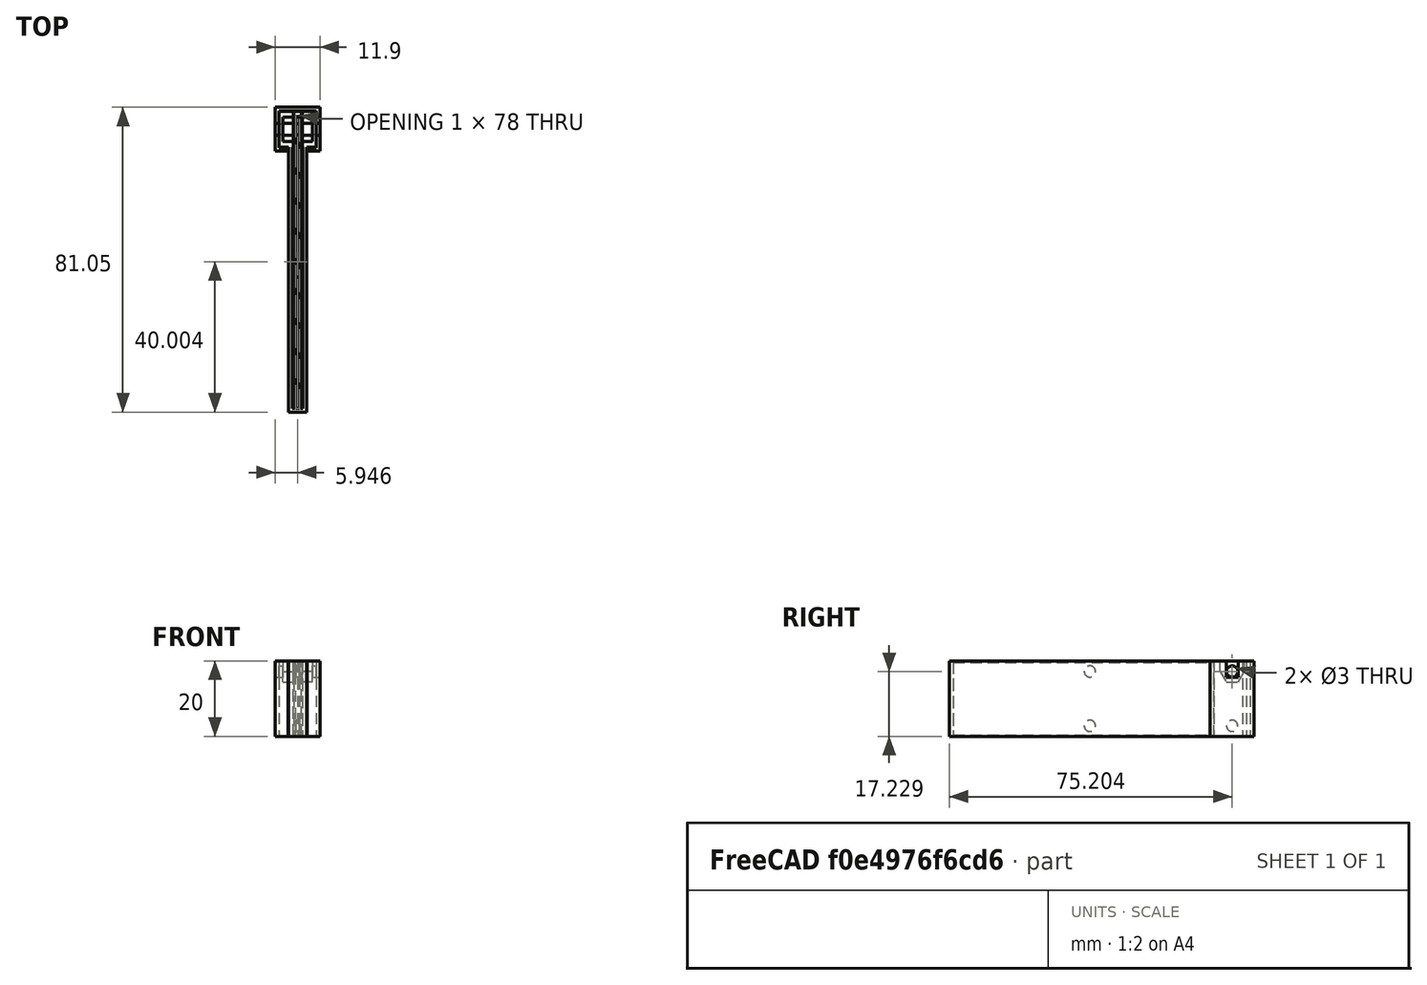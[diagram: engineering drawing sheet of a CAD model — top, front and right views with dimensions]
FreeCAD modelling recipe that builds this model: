
FCSTD DOCUMENT  (FreeCAD 0.20R29177 +233 (Git))
Label: capacitor
License: All rights reserved
LicenseURL: http://en.wikipedia.org/wiki/All_rights_reserved
objects: Part::Part2DObjectPython×31, Part::Extrusion×30, Part::Cut×20, Part::MultiFuse×7, Part::Refine×2, Part::Feature×2, Part::FeaturePython×1
note: 93 computed .brp shape members not serialized (recipe doc carries the construction recipe); baked Part::Feature solids carry a one-line shape summary decoded from their .brp

FEATURE [Part::Part2DObjectPython] Rectangle  # Draft 2D object (typed FeaturePython)
  Area = 1600
  ChamferSize = 0
  Columns = 1
  FilletRadius = 0
  Height = 80
  Length = 20
  MakeFace = true
  Placement = pos=(-3.02724,-4.37282,1) rot=(0,0,1;0rad)
  Rows = 1
FEATURE [Part::Part2DObjectPython] Rectangle001  # Draft 2D object (typed FeaturePython)
  Area = 1804
  ChamferSize = 0
  Columns = 1
  FilletRadius = 0
  Height = 82
  Length = 22
  MakeFace = true
  Placement = pos=(-4.02724,-5.37282,0) rot=(0,0,1;0rad)
  Rows = 1
FEATURE [Part::Part2DObjectPython] Rectangle002  # Draft 2D object (typed FeaturePython)
  Area = 400
  ChamferSize = 0
  Columns = 1
  FilletRadius = 0
  Height = 20
  Length = 20
  MakeFace = true
  Placement = pos=(46.4257,-3.50556,0.5) rot=(0,0,1;0rad)
  Rows = 1
FEATURE [Part::Extrusion] Extrusion002
  Base = -> Rectangle002
  Dir = (0,0,-80)
  DirMode = 0
  FaceMakerClass = Part::FaceMakerBullseye
  LengthFwd = 0
  LengthRev = 0
  Solid = true
  Symmetric = false
FEATURE [Part::Part2DObjectPython] Rectangle004  # Draft 2D object (typed FeaturePython)
  Area = 6
  ChamferSize = 0
  Columns = 1
  FilletRadius = 0
  Height = 30
  Length = 0.2
  MakeFace = true
  Placement = pos=(51.3257,-13.5056,0.5) rot=(0,0,1;0rad)
  Rows = 1
FEATURE [Part::Part2DObjectPython] Clone2D  label="Rectangle004 (2D)"  # Draft 2D object (typed FeaturePython)
  Fuse = false
  Objects = -> [Rectangle004]
  Placement = pos=(53.5257,-13.5056,0.5) rot=(0,0,1;0rad)
  Scale = (1,1,1)
FEATURE [Part::Extrusion] Extrusion003
  Base = -> Rectangle004
  Dir = (0,0,-79)
  DirMode = 0
  FaceMakerClass = Part::FaceMakerBullseye
  LengthFwd = 0
  LengthRev = 0
  Solid = true
  Symmetric = false
FEATURE [Part::Extrusion] Extrusion004
  Base = -> Clone2D
  Dir = (0,0,-79)
  DirMode = 0
  FaceMakerClass = Part::FaceMakerBullseye
  LengthFwd = 0
  LengthRev = 0
  Solid = true
  Symmetric = false
FEATURE [Part::Cut] Cut001
  Base = -> Extrusion002
  Tool = -> Extrusion004
FEATURE [Part::Cut] Cut002
  Base = -> Cut001
  Tool = -> Extrusion003
FEATURE [Part::Part2DObjectPython] Rectangle005  # Draft 2D object (typed FeaturePython)
  Area = 200.96
  ChamferSize = 0
  Columns = 1
  FilletRadius = 0
  Height = 200.96
  Length = 1
  MakeFace = true
  Placement = pos=(53.0257,101.974,0.5) rot=(0,0,1;3.14159rad)
  Rows = 1
FEATURE [Part::Extrusion] Extrusion005
  Base = -> Rectangle005
  Dir = (0,0,-79)
  DirMode = 0
  FaceMakerClass = Part::FaceMakerBullseye
  LengthFwd = 0
  LengthRev = 0
  Solid = true
  Symmetric = false
FEATURE [Part::Cut] Cut003
  Base = -> Cut002
  Tool = -> Extrusion005
FEATURE [Part::Part2DObjectPython] Rectangle006  # Draft 2D object (typed FeaturePython)
  Area = 20
  ChamferSize = 0
  Columns = 1
  FilletRadius = 0
  Height = 1
  Length = 20
  MakeFace = true
  Placement = pos=(53.0257,-3.50556,0.5) rot=(0,0,1;1.5708rad)
  Rows = 1
FEATURE [Part::Part2DObjectPython] Rectangle007  # Draft 2D object (typed FeaturePython)
  Area = 2
  ChamferSize = 0
  Columns = 1
  FilletRadius = 0
  Height = 2
  Length = 1
  MakeFace = true
  Placement = pos=(52.0257,-3.50556,-1.5) rot=(1,0,0;1.5708rad)
  Rows = 1
FEATURE [Part::Part2DObjectPython] Wire  # Draft 2D object (typed FeaturePython)
  Area = 0.5
  ChamferSize = 0
  Closed = true
  End = (53.0257,-3.50556,-1.5)
  FilletRadius = 0
  Length = 3.23607
  MakeFace = true
  Placement = pos=(52.0257,-3.50556,-1.5) rot=(1,0,0;1.5708rad)
  Points = (3) [(0,0,0),(0.5,1,0),(1,0,0)]
  Start = (52.0257,-3.50556,-1.5)
  Subdivisions = 0
FEATURE [Part::Extrusion] Extrusion006
  Base = -> Wire
  Dir = (-4e-16,55.9863,-1.24e-14)
  DirMode = 0
  FaceMakerClass = Part::FaceMakerBullseye
  LengthFwd = 0
  LengthRev = 0
  Solid = true
  Symmetric = false
FEATURE [Part::Extrusion] Extrusion007
  Base = -> Rectangle006
  Dir = (0,0,-2)
  DirMode = 0
  FaceMakerClass = Part::FaceMakerBullseye
  LengthFwd = 0
  LengthRev = 0
  Solid = true
  Symmetric = false
FEATURE [Part::Cut] Cut004
  Base = -> Extrusion007
  Tool = -> Extrusion006
FEATURE [Part::MultiFuse] Fusion
  Shapes = -> [Cut004,Cut003]
FEATURE [Part::Part2DObjectPython] Rectangle008  # Draft 2D object (typed FeaturePython)
  Area = 156
  ChamferSize = 0
  Columns = 1
  FilletRadius = 0
  Height = 20
  Length = 7.8
  MakeFace = true
  Placement = pos=(66.4257,16.4944,0.5) rot=(0,0,1;3.14159rad)
  Rows = 1
FEATURE [Part::Extrusion] Extrusion008
  Base = -> Rectangle008
  Dir = (0,0,-104.818)
  DirMode = 0
  FaceMakerClass = Part::FaceMakerBullseye
  LengthFwd = 0
  LengthRev = 0
  Solid = true
  Symmetric = false
FEATURE [Part::Cut] Cut005
  Base = -> Fusion
  Placement = pos=(0,95.9944,-63.0056) rot=(1,0,0;4.71239rad)
  Tool = -> Extrusion008
FEATURE [Part::Part2DObjectPython] Rectangle009  # Draft 2D object (typed FeaturePython)
  Area = 1550.5
  ChamferSize = 0
  Columns = 1
  FilletRadius = 0
  Height = 103.264
  Length = 15.0148
  MakeFace = true
  Placement = pos=(33.8608,-6.76991,-59.5) rot=(0,0,1;0rad)
  Rows = 1
FEATURE [Part::Part2DObjectPython] Rectangle010  # Draft 2D object (typed FeaturePython)
  Area = 974.157
  ChamferSize = 0
  Columns = 1
  FilletRadius = 0
  Height = 103.122
  Length = 9.44666
  MakeFace = true
  Placement = pos=(56.1757,-6.62743,-59.5) rot=(0,0,1;0rad)
  Rows = 1
FEATURE [Part::Extrusion] Extrusion009
  Base = -> Rectangle009
  Dir = (-3.6e-15,-1.79e-14,-80.6023)
  DirMode = 0
  FaceMakerClass = Part::FaceMakerBullseye
  LengthFwd = 0
  LengthRev = 0
  Solid = true
  Symmetric = false
FEATURE [Part::Extrusion] Extrusion010
  Base = -> Rectangle010
  Dir = (-3.6e-15,-1.79e-14,-80.6023)
  DirMode = 0
  FaceMakerClass = Part::FaceMakerBullseye
  LengthFwd = 0
  LengthRev = 0
  Solid = true
  Symmetric = false
FEATURE [Part::Cut] Cut006
  Base = -> Cut005
  Tool = -> Extrusion009
FEATURE [Part::Cut] Cut007
  Base = -> Cut006
  Tool = -> Extrusion010
FEATURE [Part::Part2DObjectPython] Polygon  # Draft 2D object (typed FeaturePython)
  Area = 26.6043
  ChamferSize = 0
  DrawMode = 0
  FacesNumber = 6
  FilletRadius = 0
  MakeFace = true
  Placement = pos=(48.6257,91.6944,-62.2713) rot=(0.57735,0.57735,0.57735;2.0944rad)
  Radius = 3.2
FEATURE [Part::Part2DObjectPython] Clone2D001  label="Polygon (2D)"  # Draft 2D object (typed FeaturePython)
  Fuse = false
  Objects = -> [Polygon]
  Placement = pos=(56.4257,91.6944,-62.2713) rot=(0.57735,0.57735,0.57735;2.0944rad)
  Scale = (1,1,1)
FEATURE [Part::Part2DObjectPython] Rectangle011  # Draft 2D object (typed FeaturePython)
  Area = 192
  ChamferSize = 0
  Columns = 1
  FilletRadius = 0
  Height = 20
  Length = 9.6
  MakeFace = true
  Placement = pos=(56.1757,86.8944,-79.5) rot=(0.57735,0.57735,0.57735;2.0944rad)
  Rows = 1
FEATURE [Part::Part2DObjectPython] Clone2D002  label="Rectangle011 (2D)"  # Draft 2D object (typed FeaturePython)
  Fuse = false
  Objects = -> [Rectangle011]
  Placement = pos=(48.8757,86.8944,-79.5) rot=(0.57735,0.57735,0.57735;2.0944rad)
  Scale = (1,1,1)
FEATURE [Part::Extrusion] Extrusion011
  Base = -> Rectangle011
  Dir = (0.25,1e-16,0)
  DirMode = 0
  FaceMakerClass = Part::FaceMakerBullseye
  LengthFwd = 0
  LengthRev = 0
  Solid = true
  Symmetric = false
FEATURE [Part::MultiFuse] Fusion001
  Shapes = -> [Cut007,Extrusion011]
FEATURE [Part::Extrusion] Extrusion012
  Base = -> Clone2D002
  Dir = (-0.25,-1e-16,0)
  DirMode = 0
  FaceMakerClass = Part::FaceMakerBullseye
  LengthFwd = 0
  LengthRev = 0
  Solid = true
  Symmetric = false
FEATURE [Part::MultiFuse] Fusion002
  Shapes = -> [Extrusion012,Fusion001]
FEATURE [Part::Extrusion] Extrusion013
  Base = -> Clone2D001
  Dir = (-2.7,0,-6e-16)
  DirMode = 0
  FaceMakerClass = Part::FaceMakerBullseye
  LengthFwd = 0
  LengthRev = 0
  Solid = true
  Symmetric = false
FEATURE [Part::Cut] Cut008
  Base = -> Fusion002
  Tool = -> Extrusion013
FEATURE [Part::Extrusion] Extrusion014
  Base = -> Polygon
  Dir = (2.7,0,6e-16)
  DirMode = 0
  FaceMakerClass = Part::FaceMakerBullseye
  LengthFwd = 0
  LengthRev = 0
  Solid = true
  Symmetric = false
FEATURE [Part::Cut] Cut009
  Base = -> Cut008
  Tool = -> Extrusion014
FEATURE [Part::Part2DObjectPython] Rectangle012  # Draft 2D object (typed FeaturePython)
  Area = 17.7362
  ChamferSize = 0
  Columns = 1
  FilletRadius = 0
  Height = 2.77128
  Length = 6.4
  MakeFace = true
  Placement = pos=(48.6257,94.8944,-62.2713) rot=(0.57735,-0.57735,-0.57735;2.0944rad)
  Rows = 1
FEATURE [Part::Extrusion] Extrusion015
  Base = -> Rectangle012
  Dir = (2.7,0,0)
  DirMode = 0
  FaceMakerClass = Part::FaceMakerBullseye
  LengthFwd = 0
  LengthRev = 0
  Solid = true
  Symmetric = false
FEATURE [Part::Cut] Cut010
  Base = -> Cut009
  Tool = -> Extrusion015
FEATURE [Part::Part2DObjectPython] Rectangle013  # Draft 2D object (typed FeaturePython)
  Area = 17.7362
  ChamferSize = 0
  Columns = 1
  FilletRadius = 0
  Height = 2.77128
  Length = 6.4
  MakeFace = true
  Placement = pos=(56.4257,88.4944,-62.2713) rot=(0.57735,0.57735,0.57735;2.0944rad)
  Rows = 1
FEATURE [Part::Extrusion] Extrusion016
  Base = -> Rectangle013
  Dir = (-2.7,0,0)
  DirMode = 0
  FaceMakerClass = Part::FaceMakerBullseye
  LengthFwd = 0
  LengthRev = 0
  Solid = true
  Symmetric = false
FEATURE [Part::Cut] Cut011
  Base = -> Cut010
  Tool = -> Extrusion016
FEATURE [Part::Part2DObjectPython] Rectangle014  # Draft 2D object (typed FeaturePython)
  Area = 192
  ChamferSize = 0
  Columns = 1
  FilletRadius = 0
  Height = 20
  Length = 9.6
  MakeFace = true
  Placement = pos=(48.6257,96.4944,-79.5) rot=(0.57735,-0.57735,-0.57735;2.0944rad)
  Rows = 1
FEATURE [Part::Part2DObjectPython] Rectangle015  # Draft 2D object (typed FeaturePython)
  Area = 192
  ChamferSize = 0
  Columns = 1
  FilletRadius = 0
  Height = 20
  Length = 9.6
  MakeFace = true
  Placement = pos=(56.4257,96.4944,-79.5) rot=(0.57735,-0.57735,-0.57735;2.0944rad)
  Rows = 1
FEATURE [Part::Extrusion] Extrusion017
  Base = -> Rectangle014
  Dir = (-1,0,0)
  DirMode = 0
  FaceMakerClass = Part::FaceMakerBullseye
  LengthFwd = 0
  LengthRev = 0
  Solid = true
  Symmetric = false
FEATURE [Part::Extrusion] Extrusion018
  Base = -> Rectangle015
  Dir = (1,0,0)
  DirMode = 0
  FaceMakerClass = Part::FaceMakerBullseye
  LengthFwd = 0
  LengthRev = 0
  Solid = true
  Symmetric = false
FEATURE [Part::Part2DObjectPython] Circle  # Draft 2D object (typed FeaturePython)
  Area = 7.06858
  FirstAngle = 0
  LastAngle = 0
  MakeFace = true
  Placement = pos=(48.6257,91.6944,-62.2713) rot=(0.57735,-0.57735,-0.57735;2.0944rad)
  Radius = 1.5
FEATURE [Part::Extrusion] Extrusion019
  Base = -> Circle
  Dir = (-18.8711,0,0)
  DirMode = 0
  FaceMakerClass = Part::FaceMakerBullseye
  LengthFwd = 0
  LengthRev = 0
  Solid = true
  Symmetric = false
FEATURE [Part::FeaturePython] Clone  label="Extrusion020"  # Draft clone (typed FeaturePython)
  AttacherType = Attacher::AttachEngine3D
  Fuse = false
  Objects = -> [Extrusion019]
  Placement = pos=(26.6711,0,-7.11e-14) rot=(0,0,1;0rad)
  Scale = (1,1,1)
FEATURE [Part::Cut] Cut012
  Base = -> Extrusion018
  Tool = -> Clone
FEATURE [Part::Cut] Cut013
  Base = -> Extrusion017
  Tool = -> Extrusion019
FEATURE [Part::MultiFuse] Fusion003
  Shapes = -> [Cut012,Cut013,Cut011]
FEATURE [Part::Refine] Fusion003001
  Source = -> Fusion003
FEATURE [Part::Part2DObjectPython] Circle001  # Draft 2D object (typed FeaturePython)
  Area = 7.06858
  FirstAngle = 0
  LastAngle = 0
  MakeFace = true
  Placement = pos=(51.5257,91.6944,-62.2713) rot=(0.57735,-0.57735,-0.57735;2.0944rad)
  Radius = 1.5
FEATURE [Part::Extrusion] Extrusion020  label="Extrusion021"
  Base = -> Circle001
  Dir = (1.5,0,0)
  DirMode = 0
  FaceMakerClass = Part::FaceMakerBullseye
  LengthFwd = 0
  LengthRev = 0
  Solid = true
  Symmetric = false
FEATURE [Part::MultiFuse] Fusion003002
  Shapes = -> [Fusion003001,Extrusion020]
FEATURE [Part::Part2DObjectPython] Circle002  # Draft 2D object (typed FeaturePython)
  Area = 7.06858
  FirstAngle = 0
  LastAngle = 0
  MakeFace = true
  Placement = pos=(52.0257,53.8444,-62.2713) rot=(0.57735,-0.57735,-0.57735;2.0944rad)
  Radius = 1.5
FEATURE [Part::Part2DObjectPython] Clone2D004  label="Circle002 (2D)"  # Draft 2D object (typed FeaturePython)
  Fuse = false
  Objects = -> [Circle002]
  Placement = pos=(52.0257,53.8444,-76.7287) rot=(0.57735,-0.57735,-0.57735;2.0944rad)
  Scale = (1,1,1)
FEATURE [Part::Extrusion] Extrusion
  Base = -> Clone2D004
  Dir = (1,0,0)
  DirMode = 0
  FaceMakerClass = Part::FaceMakerBullseye
  LengthFwd = 0
  LengthRev = 0
  Solid = true
  Symmetric = false
FEATURE [Part::Extrusion] Extrusion021  label="Extrusion022"
  Base = -> Circle002
  Dir = (1,0,0)
  DirMode = 0
  FaceMakerClass = Part::FaceMakerBullseye
  LengthFwd = 0
  LengthRev = 0
  Solid = true
  Symmetric = false
FEATURE [Part::MultiFuse] Fusion003003
  Shapes = -> [Extrusion021,Extrusion,Fusion003002]
FEATURE [Part::Part2DObjectPython] Rectangle016  # Draft 2D object (typed FeaturePython)
  Area = 48.58
  ChamferSize = 0
  Columns = 1
  FilletRadius = 0
  Height = 69.4
  Length = 0.7
  MakeFace = true
  Placement = pos=(53.2757,86.8944,-79.5) rot=(1,0,0;3.14159rad)
  Rows = 1
FEATURE [Part::Extrusion] Extrusion022  label="Extrusion023"
  Base = -> Rectangle016
  Dir = (-4e-16,1e-16,0.3)
  DirMode = 0
  FaceMakerClass = Part::FaceMakerBullseye
  LengthFwd = 0
  LengthRev = 0
  Solid = true
  Symmetric = false
FEATURE [Part::Cut] Cut
  Base = -> Fusion003003
  Tool = -> Extrusion022
FEATURE [Part::Part2DObjectPython] Rectangle017  # Draft 2D object (typed FeaturePython)
  Area = 48.58
  ChamferSize = 0
  Columns = 1
  FilletRadius = 0
  Height = 69.4
  Length = 0.7
  MakeFace = true
  Placement = pos=(51.0757,86.8944,-79.5) rot=(1,0,0;3.14159rad)
  Rows = 1
FEATURE [Part::Extrusion] Extrusion023  label="Extrusion024"
  Base = -> Rectangle017
  Dir = (-4e-16,1e-16,0.3)
  DirMode = 0
  FaceMakerClass = Part::FaceMakerBullseye
  LengthFwd = 0
  LengthRev = 0
  Solid = true
  Symmetric = false
FEATURE [Part::Cut] Cut014
  Base = -> Cut
  Tool = -> Extrusion023
FEATURE [Part::Part2DObjectPython] Rectangle018  # Draft 2D object (typed FeaturePython)
  Area = 48.58
  ChamferSize = 0
  Columns = 1
  FilletRadius = 0
  Height = 69.4
  Length = 0.7
  MakeFace = true
  Placement = pos=(53.2757,86.8944,-59.5) rot=(1,0,0;3.14159rad)
  Rows = 1
FEATURE [Part::Part2DObjectPython] Clone2D008  label="Rectangle018 (2D)"  # Draft 2D object (typed FeaturePython)
  Fuse = false
  Objects = -> [Rectangle018]
  Placement = pos=(51.0757,86.8944,-59.5) rot=(1,0,0;3.14159rad)
  Scale = (1,1,1)
FEATURE [Part::Extrusion] Extrusion024  label="Extrusion025"
  Base = -> Rectangle018
  Dir = (5e-16,-1e-16,-0.4)
  DirMode = 0
  FaceMakerClass = Part::FaceMakerBullseye
  LengthFwd = 0
  LengthRev = 0
  Solid = true
  Symmetric = false
FEATURE [Part::Extrusion] Extrusion025  label="Extrusion026"
  Base = -> Clone2D008
  Dir = (5e-16,-1e-16,-0.4)
  DirMode = 0
  FaceMakerClass = Part::FaceMakerBullseye
  LengthFwd = 0
  LengthRev = 0
  Solid = true
  Symmetric = false
FEATURE [Part::Cut] Cut015
  Base = -> Cut014
  Tool = -> Extrusion024
FEATURE [Part::Cut] Cut016
  Base = -> Cut015
  Tool = -> Extrusion025
FEATURE [Part::Feature] Face
  shape: bbox 3e-07 x 70.4 x 20 mm, 1 faces, 0 solids (baked)
FEATURE [Part::Extrusion] Extrusion026  label="Extrusion027"
  Base = -> Face
  Dir = (1.2,0,-1e-16)
  DirMode = 0
  FaceMakerClass = Part::FaceMakerBullseye
  LengthFwd = 0
  LengthRev = 0
  Solid = true
  Symmetric = false
FEATURE [Part::Cut] Cut017
  Base = -> Cut016
  Tool = -> Extrusion026
FEATURE [Part::Feature] Face001
  shape: bbox 3e-07 x 70.4 x 20 mm, 1 faces, 0 solids (baked)
FEATURE [Part::Extrusion] Extrusion027  label="Extrusion028"
  Base = -> Face001
  Dir = (-1.2,0,1e-16)
  DirMode = 0
  FaceMakerClass = Part::FaceMakerBullseye
  LengthFwd = 0
  LengthRev = 0
  Solid = true
  Symmetric = false
FEATURE [Part::Cut] Cut018
  Base = -> Cut017
  Tool = -> Extrusion027
FEATURE [Part::Refine] Cut018001
  Source = -> Cut018
FEATURE [Part::Part2DObjectPython] Wire001  # Draft 2D object (typed FeaturePython)
  Area = 38.1
  ChamferSize = 0
  Closed = true
  End = (55.0757,86.8444,-59.5)
  FilletRadius = 0
  Length = 78.2
  MakeFace = true
  Placement = pos=(55.0757,85.8444,-59.5) rot=(0,0,1;0rad)
  Points = (12) [(0,0,0),(3.4,0,0),(3.4,11.7,2.13163e-14),(-8.5,11.7,2.13163e-14),(-8.5,0,0),(-5.1,0,0),(-5.1,1,-1.27898e-13),(-7.5,1,-6.39488e-14),+4 more]
  Start = (55.0757,85.8444,-59.5)
  Subdivisions = 0
FEATURE [Part::Extrusion] Extrusion028  label="Extrusion029"
  Base = -> Wire001
  Dir = (5e-15,9.29e-14,-20)
  DirMode = 0
  FaceMakerClass = Part::FaceMakerBullseye
  LengthFwd = 0
  LengthRev = 0
  Solid = true
  Symmetric = false
FEATURE [Part::Part2DObjectPython] Rectangle019  # Draft 2D object (typed FeaturePython)
  Area = 13.76
  ChamferSize = 0
  Columns = 1
  FilletRadius = 0
  Height = 4.3
  Length = 3.2
  MakeFace = true
  Placement = pos=(46.5757,93.2944,-63.8) rot=(0.57735,-0.57735,-0.57735;2.0944rad)
  Rows = 1
FEATURE [Part::Extrusion] Extrusion029  label="Extrusion030"
  Base = -> Rectangle019
  Dir = (17.8604,2.38e-14,3.17e-14)
  DirMode = 0
  FaceMakerClass = Part::FaceMakerBullseye
  LengthFwd = 0
  LengthRev = 0
  Solid = true
  Symmetric = false
FEATURE [Part::Cut] Cut018002
  Base = -> Extrusion028
  Tool = -> Extrusion029
FEATURE [Part::Part2DObjectPython] Circle003  # Draft 2D object (typed FeaturePython)
  Area = 7.06858
  FirstAngle = 0
  LastAngle = 0
  MakeFace = true
  Placement = pos=(53.0257,91.6944,-76.7287) rot=(0.57735,-0.57735,-0.57735;2.0944rad)
  Radius = 1.5
FEATURE [Part::Extrusion] Extrusion030  label="Extrusion031"
  Base = -> Circle003
  Dir = (-1,0,0)
  DirMode = 0
  FaceMakerClass = Part::FaceMakerBullseye
  LengthFwd = 0
  LengthRev = 0
  Solid = true
  Symmetric = false
FEATURE [Part::MultiFuse] Fusion003004
  Shapes = -> [Extrusion030,Cut018001]
